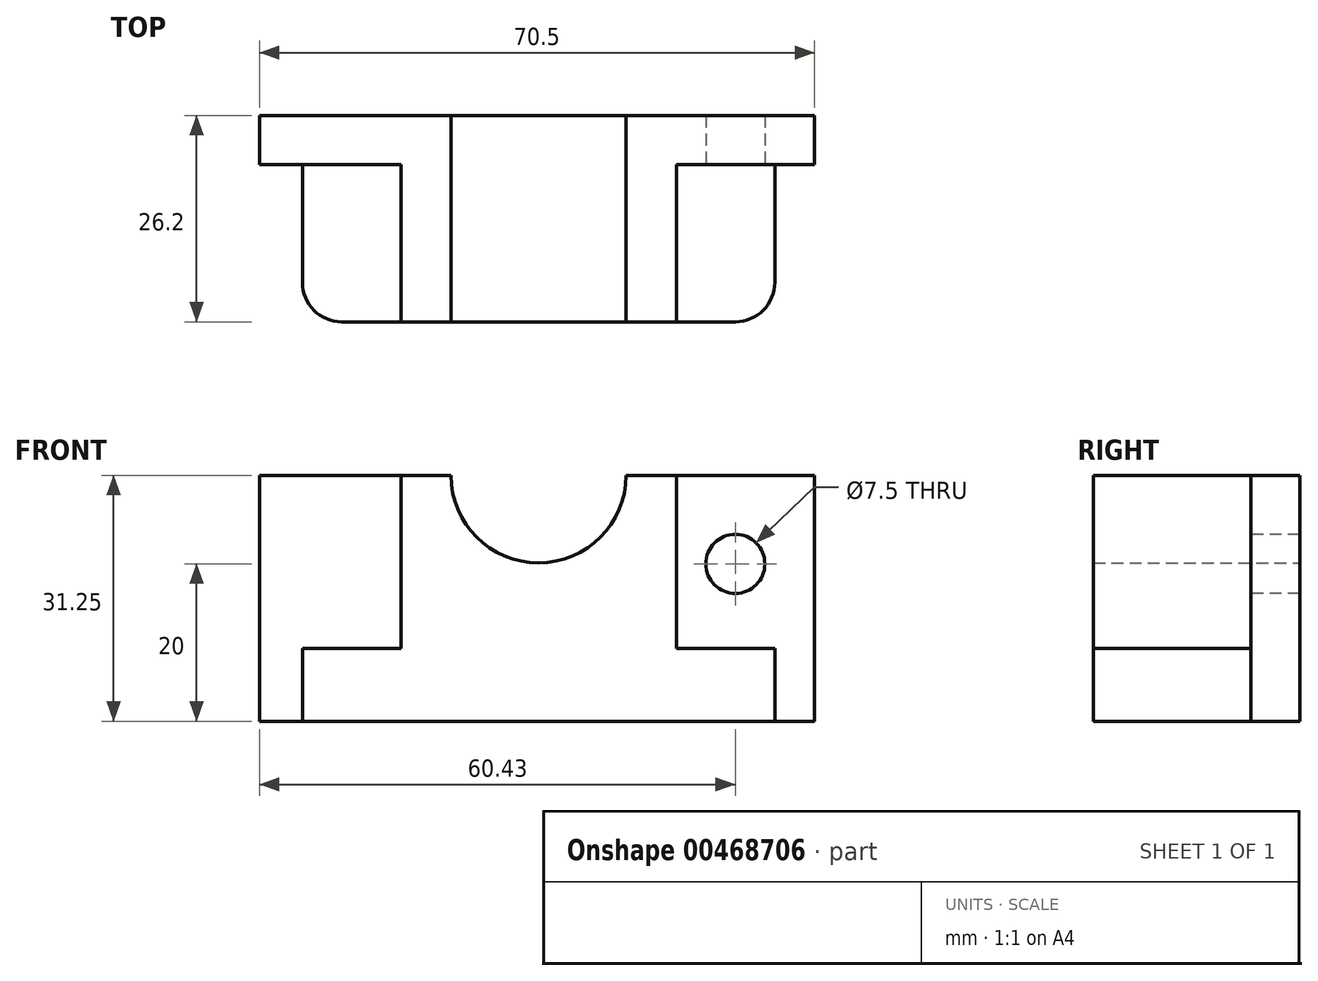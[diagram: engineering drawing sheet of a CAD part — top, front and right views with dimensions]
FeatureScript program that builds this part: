
annotation { "Feature Type Name" : "Feature", "Feature Type Description" : "" }
export const myFeature = defineFeature(function(context is Context, id is Id, definition is map)
    precondition{}
    {
        {
            var Q0;
            Q0=qCreatedBy(makeId("Front.planeOp"),FACE);
            var sketch = newSketch(context, id + "F0", { "sketchPlane" : qUnion([Q0])});
            skLineSegment(sketch, "E0.top", {"start": v(-35.43, -15.99) * mm, "end": v(35.07, -15.99) * mm});
            skLineSegment(sketch, "E0.left", {"start": v(-35.43, 15.26) * mm, "end": v(-35.43, -15.99) * mm});
            skLineSegment(sketch, "E0.right", {"start": v(35.07, 15.26) * mm, "end": v(35.07, -15.99) * mm});
            skPoint(sketch, "E1", {"position": v(0, 15.28) * mm});
            skLineSegment(sketch, "E2", {"start": v(-35.43, 15.26) * mm, "end": v(-11.12, 15.26) * mm});
            skArc(sketch, "E3", {"start": v(-11.12, 15.26) * mm, "mid": v(0, 4.15) * mm, "end": v(11.12, 15.26) * mm});
            skLineSegment(sketch, "E4.trimOffspring", {"start": v(11.12, 15.26) * mm, "end": v(35.07, 15.26) * mm});
            skSolve(sketch);
        }
        {
            var Q0;
            Q0=makeQuery(id+"F0.imprint","IMPRINT",FACE,{"disambiguationData":[TD([[makeQuery(id+"F0.imprint","IMPRINT",EDGE,{"derivedFrom":sQuery(id+"F0.wireOp",EDGE,"E0.top")}),1.0]])]});
            extrude(context, id + "F1", {"entities" : qUnion([Q0]), "endBound" : BoundingType.SYMMETRIC, "depth" : 6.2 * mm});
        }
        {
            var Q0;
            Q0=makeQuery(id+"F1.opExtrude","CAP_FACE",FACE,{"disambiguationData":[OSD([sQuery(id+"F0.wireOp",EDGE,"E0.top"),sQuery(id+"F0.wireOp",EDGE,"E0.left"),sQuery(id+"F0.wireOp",EDGE,"E0.right"),sQuery(id+"F0.wireOp",EDGE,"E2"),sQuery(id+"F0.wireOp",EDGE,"E3"),sQuery(id+"F0.wireOp",EDGE,"E4.trimOffspring")])],"isStart":false});
            var sketch = newSketch(context, id + "F2", { "sketchPlane" : qUnion([Q0])});
            skLineSegment(sketch, "E5", {"start": v(-17.5, 15.26) * mm, "end": v(-11.12, 15.26) * mm});
            skLineSegment(sketch, "E6", {"start": v(17.5, 15.26) * mm, "end": v(11.12, 15.26) * mm});
            skArc(sketch, "E7", {"start": v(-10.88, 15.26) * mm, "mid": v(0, 4.38) * mm, "end": v(10.88, 15.26) * mm});
            skPoint(sketch, "E7.centerSnap0", {"position": v(0, 4.15) * mm});
            skLineSegment(sketch, "E8", {"start": v(-11.12, 15.26) * mm, "end": v(17.5, 15.26) * mm, "construction": true});
            skLineSegment(sketch, "E9", {"start": v(-17.5, 15.26) * mm, "end": v(-17.5, -6.74) * mm});
            skLineSegment(sketch, "E10", {"start": v(17.5, -6.74) * mm, "end": v(17.5, 15.26) * mm});
            skLineSegment(sketch, "E11", {"start": v(-17.5, -6.74) * mm, "end": v(-30, -6.74) * mm});
            skLineSegment(sketch, "E12", {"start": v(-30, -6.74) * mm, "end": v(-30, -15.99) * mm});
            skLineSegment(sketch, "E13", {"start": v(-30, -15.99) * mm, "end": v(30, -15.99) * mm});
            skLineSegment(sketch, "E14", {"start": v(30, -15.99) * mm, "end": v(30, -6.74) * mm});
            skLineSegment(sketch, "E15", {"start": v(30, -6.74) * mm, "end": v(17.5, -6.74) * mm});
            skSolve(sketch);
        }
        {
            var Q0;
            Q0=makeQuery(id+"F2.imprint","IMPRINT",FACE,{"disambiguationData":[TD([[makeQuery(id+"F2.imprint","IMPRINT",EDGE,{"derivedFrom":sQuery(id+"F2.wireOp",EDGE,"E5")}),-1.0]])]});
            extrude(context, id + "F3", {"entities" : qUnion([Q0]), "operationType" : NewBodyOperationType.ADD, "depth" : 20 * mm});
        }
        {
            var Q0;
            Q0=makeQuery(id+"F3.opExtrude","CAP_EDGE",EDGE,{"disambiguationData":[OSD([sQuery(id+"F2.wireOp",EDGE,"E12")])],"isStart":false});
            var Q1;
            Q1=makeQuery(id+"F3.opExtrude","CAP_EDGE",EDGE,{"disambiguationData":[OSD([sQuery(id+"F2.wireOp",EDGE,"E14")])],"isStart":false});
            fillet(context, id + "F4", {"entities" : qUnion([Q0, Q1]), "radius" : 5 * mm, "tangentPropagation" : true, "allowEdgeOverflow" : false});
        }
        {
            var Q0;
            {var subQ0=sQuery(id+"F0.wireOp",EDGE,"E0.right");var subQ1=sQuery(id+"F0.wireOp",EDGE,"E4.trimOffspring");var subQ2=sQuery(id+"F0.wireOp",EDGE,"E0.top");Q0=makeQuery(id+"F3.boolean.opBoolean","SPLIT",FACE,{"disambiguationData":[TD([makeQuery(id+"F1.opExtrude","SWEPT_FACE",FACE,{"disambiguationData":[OSD([subQ0])]})])],"derivedFrom":makeQuery(id+"F1.opExtrude","CAP_FACE",FACE,{"disambiguationData":[OSD([subQ2,sQuery(id+"F0.wireOp",EDGE,"E0.left"),subQ0,sQuery(id+"F0.wireOp",EDGE,"E2"),sQuery(id+"F0.wireOp",EDGE,"E3"),subQ1])],"isStart":false})});}
            var sketch = newSketch(context, id + "F5", { "sketchPlane" : qUnion([Q0])});
            skLineSegment(sketch, "E16", {"start": v(0, 0) * mm, "end": v(0, 34.9) * mm, "construction": true});
            skLineSegment(sketch, "E17", {"start": v(25, 34.38) * mm, "end": v(25, 4.01) * mm, "construction": true});
            skLineSegment(sketch, "E18", {"start": v(19.26, 4.01) * mm, "end": v(46.56, 4.01) * mm, "construction": true});
            skPoint(sketch, "E19", {"position": v(25, 4.01) * mm});
            skCircle(sketch, "E20", {"center": v(25, 4.01) * mm, "radius": 3.75 * mm});
            skCircle(sketch, "E21.MirrorC", {"center": v(-25, 4.01) * mm, "radius": 3.75 * mm});
            skLineSegment(sketch, "E22.MirrorCS", {"start": v(-25, 34.38) * mm, "end": v(-25, 4.01) * mm, "construction": true});
            skLineSegment(sketch, "E23.MirrorCS", {"start": v(-19.26, 4.01) * mm, "end": v(-46.56, 4.01) * mm, "construction": true});
            skSolve(sketch);
        }
        {
            var Q0;
            Q0=makeQuery(id+"F5.imprint","IMPRINT",FACE,{"disambiguationData":[TD([[makeQuery(id+"F5.imprint","IMPRINT",EDGE,{"derivedFrom":sQuery(id+"F5.wireOp",EDGE,"E21.MirrorC")}),-1.0]])]});
            var Q1;
            Q1=makeQuery(id+"F5.imprint","IMPRINT",FACE,{"disambiguationData":[TD([[makeQuery(id+"F5.imprint","IMPRINT",EDGE,{"derivedFrom":sQuery(id+"F5.wireOp",EDGE,"E20")}),1.0]])]});
            extrude(context, id + "F6", {"entities" : qUnion([Q0, Q1]), "operationType" : NewBodyOperationType.REMOVE, "oppositeDirection" : true, "depth" : 25.4 * mm});
        }
    });
